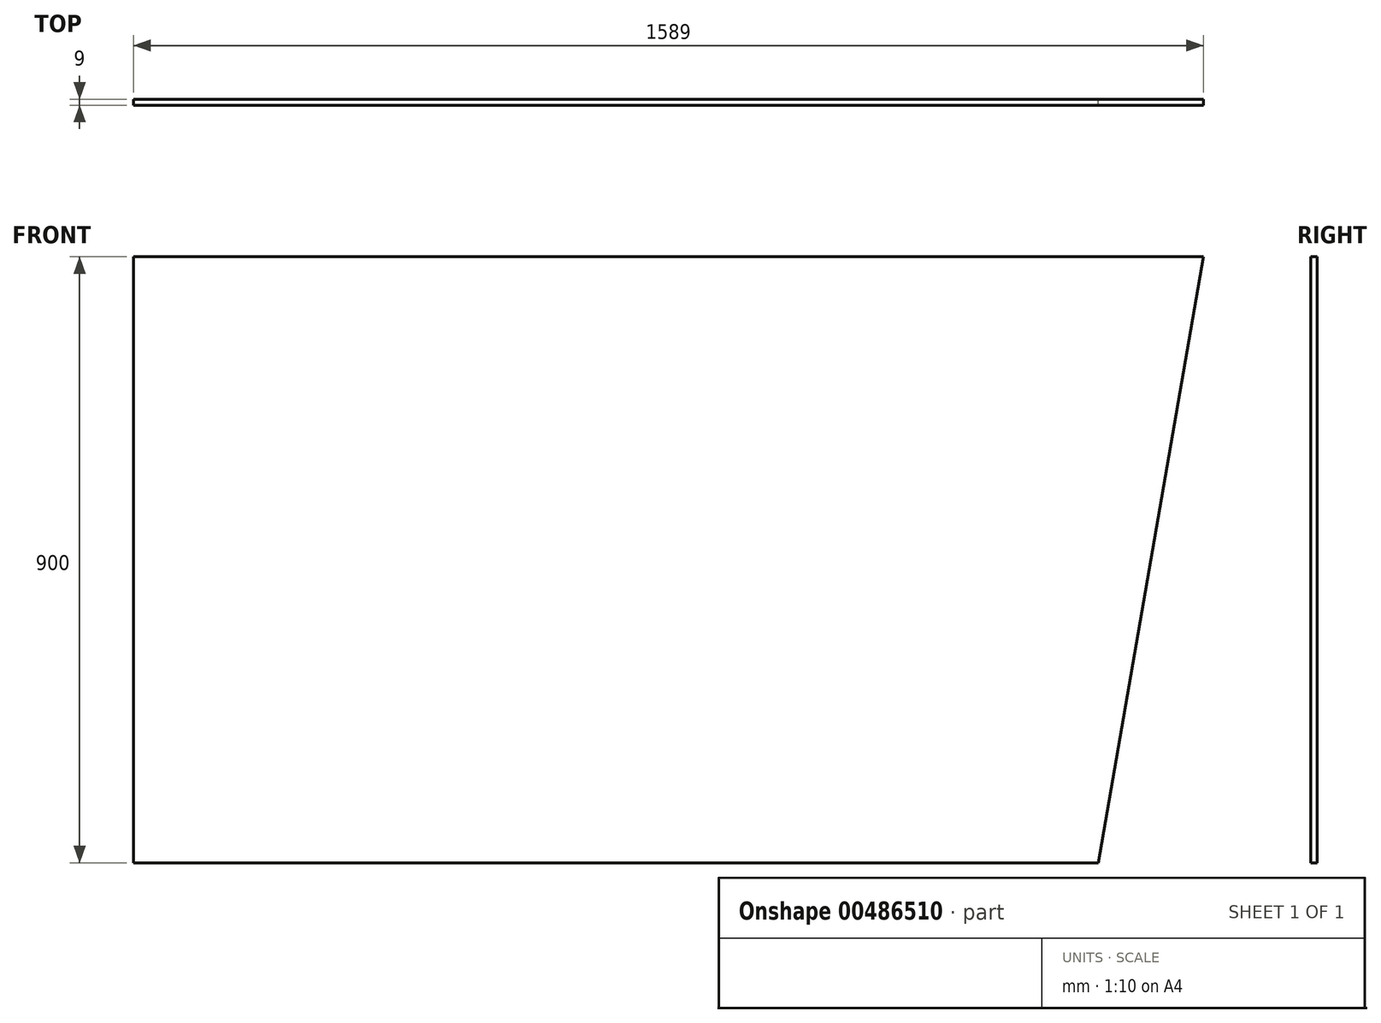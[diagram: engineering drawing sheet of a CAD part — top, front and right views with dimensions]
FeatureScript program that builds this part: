
annotation { "Feature Type Name" : "Feature", "Feature Type Description" : "" }
export const myFeature = defineFeature(function(context is Context, id is Id, definition is map)
    precondition{}
    {
        {
            var Q0;
            Q0=qCreatedBy(makeId("Front.planeOp"),FACE);
            var sketch = newSketch(context, id + "F0", { "sketchPlane" : qUnion([Q0])});
            skLineSegment(sketch, "E0", {"start": v(0, 900) * mm, "end": v(0, 0) * mm});
            skLineSegment(sketch, "E1.MirrorCS", {"start": v(0, 900) * mm, "end": v(1593, 900) * mm});
            skLineSegment(sketch, "E2.MirrorCS", {"start": v(1589, 900) * mm, "end": v(1433, 0) * mm});
            skLineSegment(sketch, "E3.MirrorCS", {"start": v(1433, 0) * mm, "end": v(0, 0) * mm});
            skSolve(sketch);
        }
        {
            var Q0;
            Q0=makeQuery(id+"F0.imprint","IMPRINT",FACE,{"disambiguationData":[TD([[makeQuery(id+"F0.imprint","IMPRINT",EDGE,{"derivedFrom":sQuery(id+"F0.wireOp",EDGE,"E0")}),1.0]])]});
            extrude(context, id + "F1", {"entities" : qUnion([Q0]), "depth" : 9 * mm, "offsetDistance" : 25 * mm});
        }
    });
